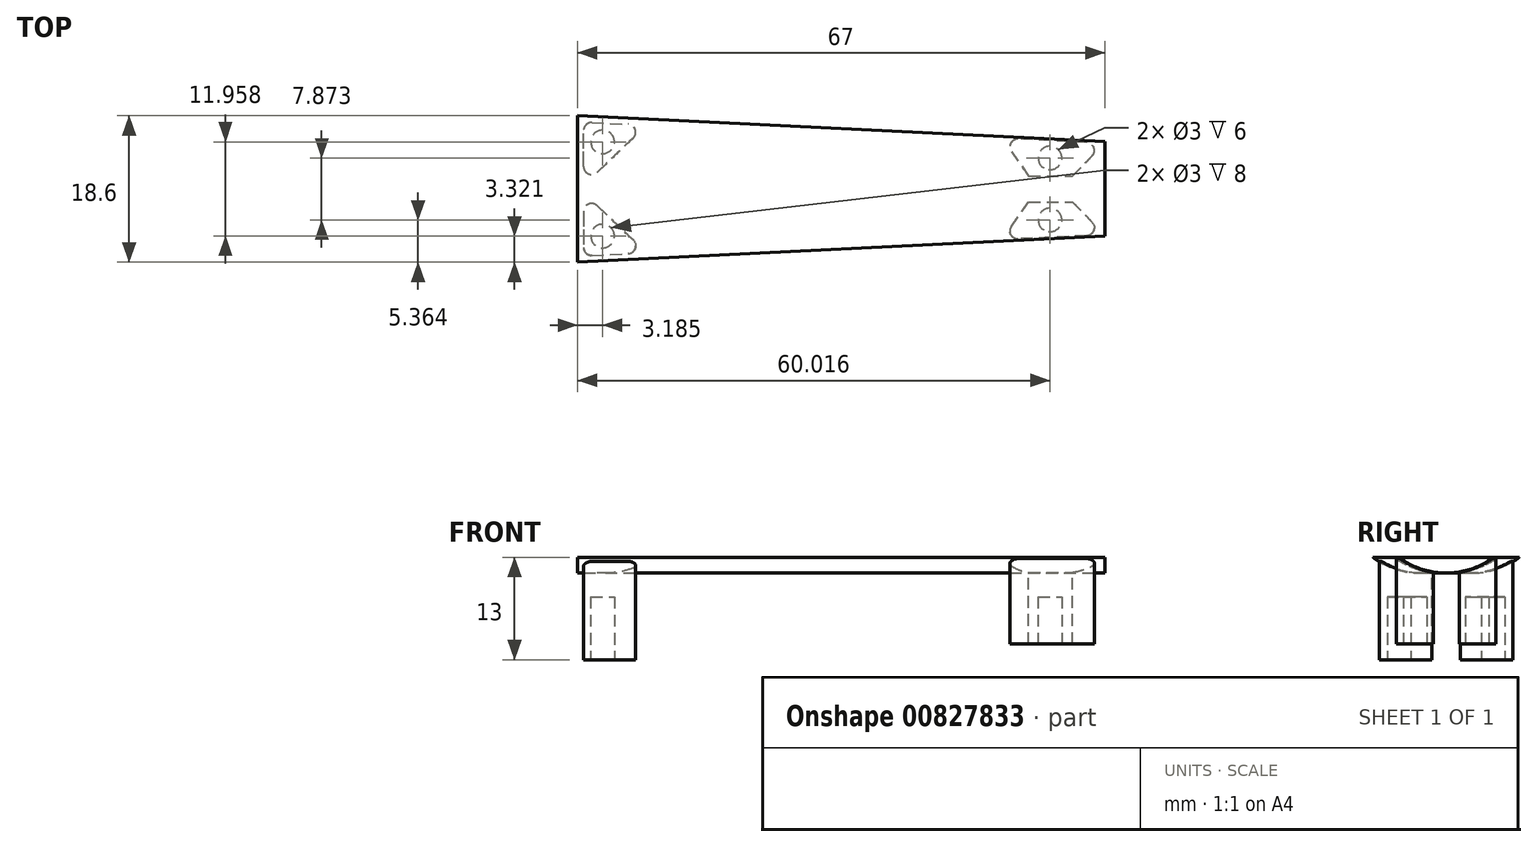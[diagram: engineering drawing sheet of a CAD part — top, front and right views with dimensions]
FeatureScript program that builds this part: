
annotation { "Feature Type Name" : "Feature", "Feature Type Description" : "" }
export const myFeature = defineFeature(function(context is Context, id is Id, definition is map)
    precondition{}
    {
        {
            var Q0;
            Q0=qCreatedBy(makeId("Top.planeOp"),FACE);
            var sketch = newSketch(context, id + "F0", { "sketchPlane" : qUnion([Q0])});
            skLineSegment(sketch, "E0", {"start": v(0, 0) * mm, "end": v(0, 9.3) * mm});
            skLineSegment(sketch, "E1", {"start": v(0, 9.3) * mm, "end": v(67, 6) * mm});
            skLineSegment(sketch, "E2", {"start": v(67, 6) * mm, "end": v(67, 0) * mm});
            skLineSegment(sketch, "E3", {"start": v(67, 0) * mm, "end": v(0, 0) * mm});
            skSolve(sketch);
        }
        {
            var Q0;
            Q0=qSketchRegion(id+"F0",true);
            extrude(context, id + "F1", {"entities" : qUnion([Q0]), "depth" : 2 * mm, "offsetDistance" : 25 * mm});
        }
        {
            var Q0;
            Q0=makeQuery(id+"F1.opExtrude","CAP_FACE",FACE,{"disambiguationData":[OSD([sQuery(id+"F0.wireOp",EDGE,"E0"),sQuery(id+"F0.wireOp",EDGE,"E1"),sQuery(id+"F0.wireOp",EDGE,"E2"),sQuery(id+"F0.wireOp",EDGE,"E3")])],"isStart":false});
            var sketch = newSketch(context, id + "F2", { "sketchPlane" : qUnion([Q0])});
            skLineSegment(sketch, "E4", {"start": v(0.79, 0.5) * mm, "end": v(0.79, 8.5) * mm});
            skLineSegment(sketch, "E5", {"start": v(0.79, 8.5) * mm, "end": v(8.78, 8.1) * mm});
            skLineSegment(sketch, "E6", {"start": v(8.78, 8.1) * mm, "end": v(0.79, 0.5) * mm});
            skLineSegment(sketch, "E7", {"start": v(66.9, 5.8) * mm, "end": v(53.92, 6.44) * mm});
            skLineSegment(sketch, "E8", {"start": v(53.92, 6.44) * mm, "end": v(57.3, 1.65) * mm});
            skLineSegment(sketch, "E9", {"start": v(57.3, 1.65) * mm, "end": v(62.9, 1.65) * mm});
            skLineSegment(sketch, "E10", {"start": v(62.9, 1.65) * mm, "end": v(66.9, 5.8) * mm});
            skSolve(sketch);
        }
        {
            var Q0;
            Q0=makeQuery(id+"F2.imprint","IMPRINT",FACE,{"disambiguationData":[TD([[makeQuery(id+"F2.imprint","IMPRINT",EDGE,{"derivedFrom":sQuery(id+"F2.wireOp",EDGE,"E4")}),-1.0]])]});
            extrude(context, id + "F3", {"entities" : qUnion([Q0]), "operationType" : NewBodyOperationType.ADD, "oppositeDirection" : true, "depth" : 13 * mm, "offsetDistance" : 25 * mm});
        }
        {
            var Q0;
            Q0=makeQuery(id+"F2.imprint","IMPRINT",FACE,{"disambiguationData":[TD([[makeQuery(id+"F2.imprint","IMPRINT",EDGE,{"derivedFrom":sQuery(id+"F2.wireOp",EDGE,"E7")}),1.0]])]});
            extrude(context, id + "F4", {"entities" : qUnion([Q0]), "operationType" : NewBodyOperationType.ADD, "oppositeDirection" : true, "depth" : 11 * mm, "offsetDistance" : 25 * mm});
        }
        {
            var Q0;
            Q0=makeQuery(id+"F3.opExtrude","CAP_FACE",FACE,{"disambiguationData":[OSD([sQuery(id+"F2.wireOp",EDGE,"E4"),sQuery(id+"F2.wireOp",EDGE,"E5"),sQuery(id+"F2.wireOp",EDGE,"E6")])],"isStart":false});
            var sketch = newSketch(context, id + "F5", { "sketchPlane" : qUnion([Q0])});
            skCircle(sketch, "E11", {"center": v(3.19, -5.98) * mm, "radius": 1.5 * mm});
            skCircle(sketch, "E12", {"center": v(60.02, -3.94) * mm, "radius": 1.5 * mm});
            skSolve(sketch);
        }
        {
            var Q0;
            Q0 = qSketchRegion(id + "F5", true);
            extrude(context, id + "F6", {"entities" : qUnion([Q0]), "operationType" : NewBodyOperationType.REMOVE, "oppositeDirection" : true, "depth" : 8 * mm, "offsetDistance" : 25 * mm});
        }
        {
            var Q0;
            Q0=makeQuery(id+"F1.opExtrude","CAP_EDGE",EDGE,{"disambiguationData":[OSD([sQuery(id+"F0.wireOp",EDGE,"E1")])],"isStart":true});
            fillet(context, id + "F7", {"entities" : qUnion([Q0]), "radius" : 10 * mm, "tangentPropagation" : true, "allowEdgeOverflow" : false});
        }
        {
            var Q0;
            Q0=makeQuery(id+"F3.opExtrude","SWEPT_EDGE",EDGE,{"disambiguationData":[OSD([sQuery(id+"F2.wireOp",EDGE,"E4"),sQuery(id+"F2.wireOp",EDGE,"E5")])]});
            var Q1;
            Q1=makeQuery(id+"F3.opExtrude","SWEPT_EDGE",EDGE,{"disambiguationData":[OSD([sQuery(id+"F2.wireOp",EDGE,"E5"),sQuery(id+"F2.wireOp",EDGE,"E6")])]});
            var Q2;
            Q2=makeQuery(id+"F3.opExtrude","SWEPT_EDGE",EDGE,{"disambiguationData":[OSD([sQuery(id+"F2.wireOp",EDGE,"E4"),sQuery(id+"F2.wireOp",EDGE,"E6")])]});
            var Q3;
            Q3=makeQuery(id+"F3.opExtrude","SWEPT_EDGE",EDGE,{"disambiguationData":[OSD([sQuery(id+"F2.wireOp",EDGE,"E7"),sQuery(id+"F2.wireOp",EDGE,"E10")])]});
            var Q4;
            Q4=makeQuery(id+"F3.opExtrude","SWEPT_EDGE",EDGE,{"disambiguationData":[OSD([sQuery(id+"F2.wireOp",EDGE,"E7"),sQuery(id+"F2.wireOp",EDGE,"E8")])]});
            var Q5;
            Q5=makeQuery(id+"F3.opExtrude","SWEPT_EDGE",EDGE,{"disambiguationData":[OSD([sQuery(id+"F2.wireOp",EDGE,"E9"),sQuery(id+"F2.wireOp",EDGE,"E10")])]});
            var Q6;
            Q6=makeQuery(id+"F3.opExtrude","SWEPT_EDGE",EDGE,{"disambiguationData":[OSD([sQuery(id+"F2.wireOp",EDGE,"E8"),sQuery(id+"F2.wireOp",EDGE,"E9")])]});
            var Q7;
            Q7=makeQuery(id+"F4.opExtrude","SWEPT_EDGE",EDGE,{"disambiguationData":[OSD([sQuery(id+"F2.wireOp",EDGE,"E7"),sQuery(id+"F2.wireOp",EDGE,"E10")])]});
            var Q8;
            Q8=makeQuery(id+"F4.opExtrude","SWEPT_EDGE",EDGE,{"disambiguationData":[OSD([sQuery(id+"F2.wireOp",EDGE,"E7"),sQuery(id+"F2.wireOp",EDGE,"E8")])]});
            fillet(context, id + "F8", {"entities" : qUnion([Q0, Q1, Q2, Q3, Q4, Q5, Q6, Q7, Q8]), "radius" : 1 * mm, "tangentPropagation" : true, "allowEdgeOverflow" : false});
        }
        {
            var Q0;
            Q0=makeQuery(id+"F1.opExtrude","SWEPT_BODY",BODY,{"disambiguationData":[OSD([sQuery(id+"F0.wireOp",EDGE,"E0"),sQuery(id+"F0.wireOp",EDGE,"E1"),sQuery(id+"F0.wireOp",EDGE,"E2"),sQuery(id+"F0.wireOp",EDGE,"E3")])]});
            var Q1;
            Q1=qCreatedBy(makeId("Front.planeOp"),FACE);
            mirror(context, id + "F9", {"operationType" : NewBodyOperationType.ADD, "entities" : qUnion([Q0]), "mirrorPlane" : qUnion([Q1])});
        }
    });
